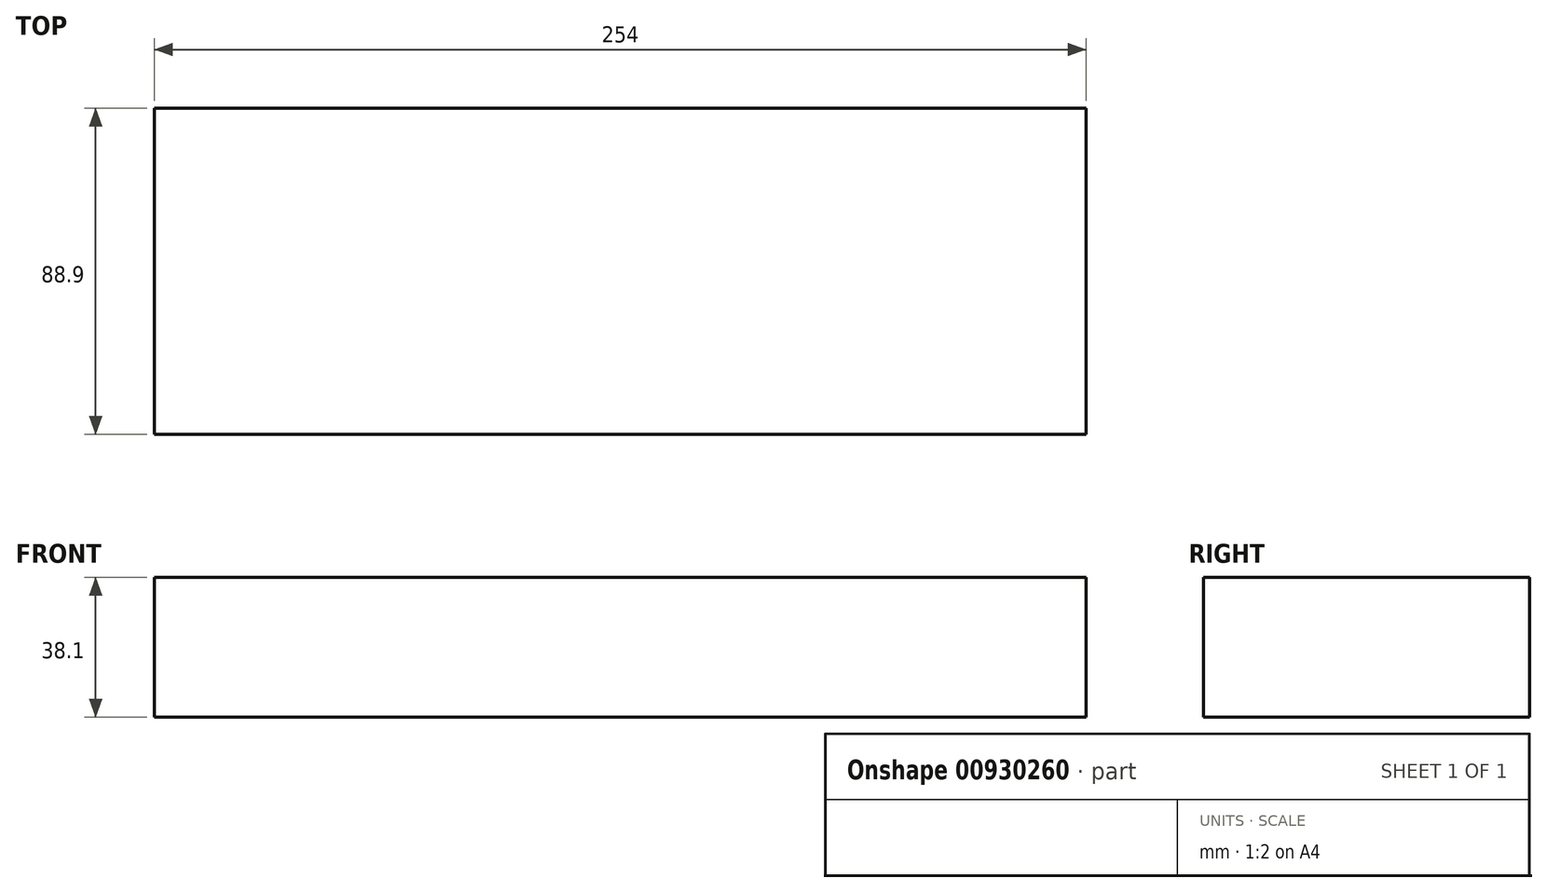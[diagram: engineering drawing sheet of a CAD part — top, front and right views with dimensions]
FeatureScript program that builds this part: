
annotation { "Feature Type Name" : "Feature", "Feature Type Description" : "" }
export const myFeature = defineFeature(function(context is Context, id is Id, definition is map)
    precondition{}
    {
        {
            var Q0;
            Q0=qCreatedBy(makeId("Right.planeOp"),FACE);
            var sketch = newSketch(context, id + "F0", { "sketchPlane" : qUnion([Q0])});
            skLineSegment(sketch, "E0.bottom", {"start": v(44.45, -19.05) * mm, "end": v(-44.45, -19.05) * mm});
            skLineSegment(sketch, "E0.top", {"start": v(44.45, 19.05) * mm, "end": v(-44.45, 19.05) * mm});
            skLineSegment(sketch, "E0.left", {"start": v(44.45, -19.05) * mm, "end": v(44.45, 19.05) * mm});
            skLineSegment(sketch, "E0.right", {"start": v(-44.45, -19.05) * mm, "end": v(-44.45, 19.05) * mm});
            skPoint(sketch, "E0.middle", {"position": v(0, 0) * mm});
            skSolve(sketch);
        }
        {
            var Q0;
            Q0=qSketchRegion(id+"F0",true);
            extrude(context, id + "F1", {"entities" : qUnion([Q0]), "endBound" : BoundingType.SYMMETRIC, "depth" : 254 * mm});
        }
    });
